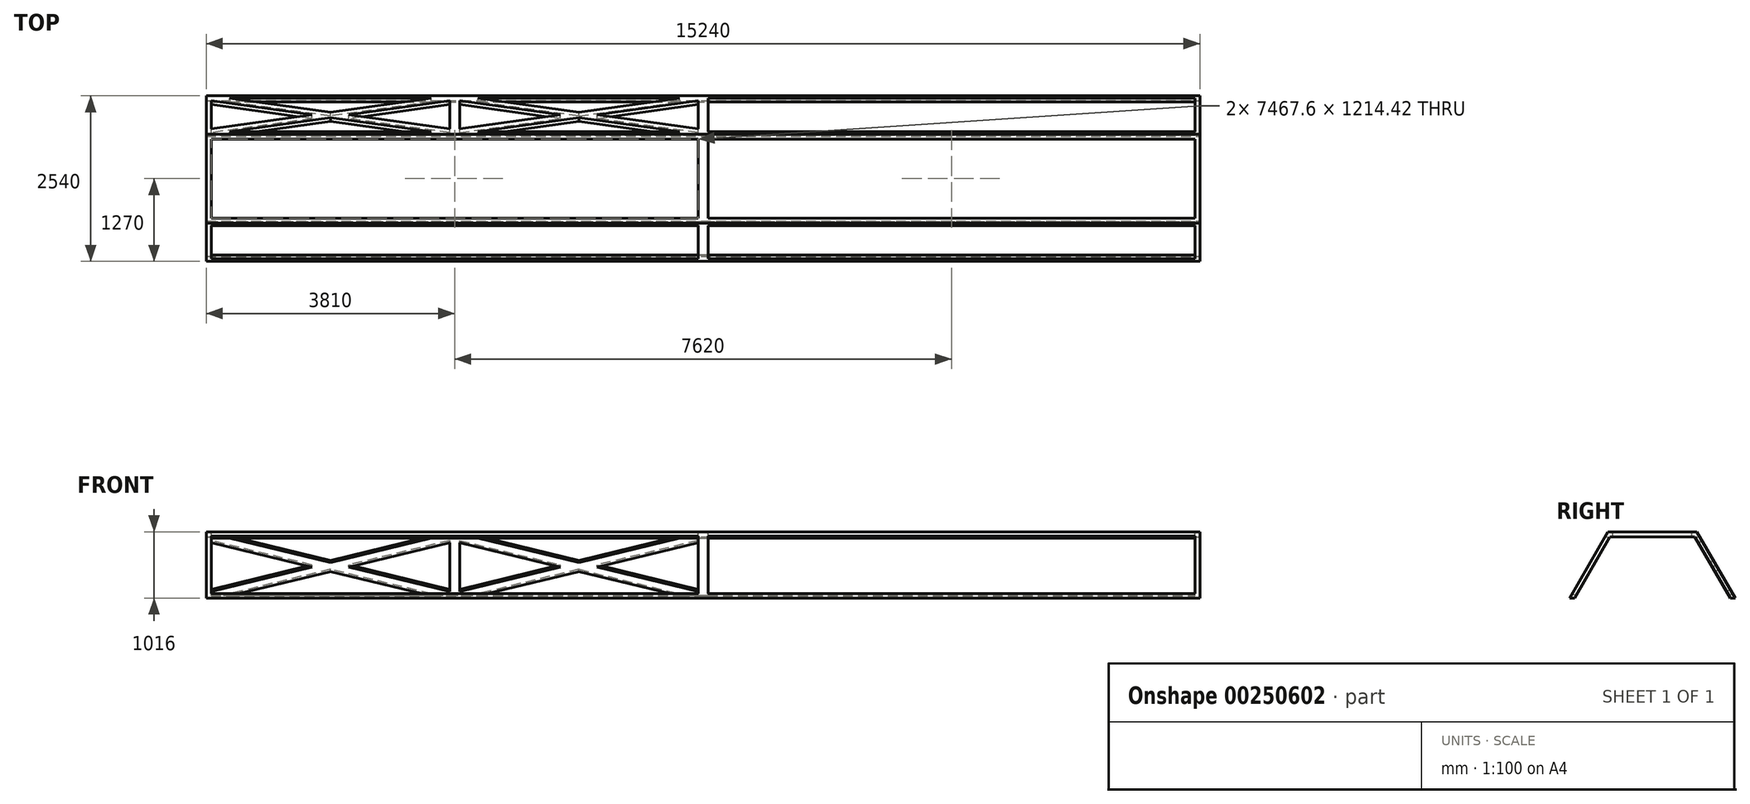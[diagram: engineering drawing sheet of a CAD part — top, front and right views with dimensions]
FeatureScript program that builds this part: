
annotation { "Feature Type Name" : "Feature", "Feature Type Description" : "" }
export const myFeature = defineFeature(function(context is Context, id is Id, definition is map)
    precondition{}
    {
        {
            var Q0;
            Q0=qCreatedBy(makeId("Right.planeOp"),FACE);
            var sketch = newSketch(context, id + "F0", { "sketchPlane" : qUnion([Q0])});
            skLineSegment(sketch, "E0", {"start": v(-627.03, 0) * mm, "end": v(-550.83, 0) * mm});
            skLineSegment(sketch, "E1", {"start": v(-627.03, 0) * mm, "end": v(-40.44, 1016) * mm});
            skLineSegment(sketch, "E2", {"start": v(-40.44, 1016) * mm, "end": v(1326.38, 1016) * mm});
            skLineSegment(sketch, "E3", {"start": v(-550.83, 0) * mm, "end": v(-8.23, 939.8) * mm});
            skLineSegment(sketch, "E4.MirrorCS", {"start": v(1836.77, 0) * mm, "end": v(1294.18, 939.8) * mm});
            skLineSegment(sketch, "E5.MirrorCS", {"start": v(1912.97, 0) * mm, "end": v(1326.38, 1016) * mm});
            skLineSegment(sketch, "E6", {"start": v(1912.97, 0) * mm, "end": v(1836.77, 0) * mm});
            skLineSegment(sketch, "E7.0", {"start": v(-8.23, 939.8) * mm, "end": v(1294.18, 939.8) * mm});
            skPoint(sketch, "E8.orphan", {"position": v(1250.18, 1016) * mm});
            skPoint(sketch, "E9.orphan", {"position": v(35.76, 1016) * mm});
            skPoint(sketch, "E10.orphan", {"position": v(642.97, 1016) * mm});
            skSolve(sketch);
        }
        {
            var Q0;
            Q0 = qSketchRegion(id + "F0", true);
            extrude(context, id + "F1", {"entities" : qUnion([Q0]), "oppositeDirection" : true, "depth" : 15240 * mm});
        }
        {
            var Q0;
            Q0=makeQuery(id+"F1.opExtrude","SWEPT_FACE",FACE,{"disambiguationData":[OSD([sQuery(id+"F0.wireOp",EDGE,"E1")])]});
            var sketch = newSketch(context, id + "F2", { "sketchPlane" : qUnion([Q0])});
            skLineSegment(sketch, "E11", {"start": v(-15240, 859.66) * mm, "end": v(0, 859.66) * mm});
            skLineSegment(sketch, "E12.0", {"start": v(-15163.8, 783.46) * mm, "end": v(-76.2, 783.46) * mm});
            skLineSegment(sketch, "E13", {"start": v(-15240, 859.66) * mm, "end": v(-15240, -313.51) * mm});
            skLineSegment(sketch, "E14.0", {"start": v(-15163.8, 783.46) * mm, "end": v(-15163.8, -237.31) * mm});
            skLineSegment(sketch, "E15", {"start": v(-15240, -313.51) * mm, "end": v(0, -313.51) * mm});
            skLineSegment(sketch, "E16.0", {"start": v(-15163.8, -237.31) * mm, "end": v(-76.2, -237.31) * mm});
            skLineSegment(sketch, "E17", {"start": v(0, 859.66) * mm, "end": v(0, -313.51) * mm});
            skLineSegment(sketch, "E18.0", {"start": v(-76.2, 783.46) * mm, "end": v(-76.2, -237.31) * mm});
            skSolve(sketch);
        }
        {
            var Q0;
            Q0=makeQuery(id+"F2.imprint","IMPRINT",FACE,{"disambiguationData":[TD([[makeQuery(id+"F2.imprint","IMPRINT",EDGE,{"derivedFrom":sQuery(id+"F2.wireOp",EDGE,"E12.0")}),-1.0]])]});
            extrude(context, id + "F3", {"entities" : qUnion([Q0]), "operationType" : NewBodyOperationType.REMOVE, "oppositeDirection" : true, "depth" : 76.2 * mm});
        }
        {
            var Q0;
            Q0=makeQuery(id+"F1.opExtrude","SWEPT_FACE",FACE,{"disambiguationData":[OSD([sQuery(id+"F0.wireOp",EDGE,"E2")])]});
            var sketch = newSketch(context, id + "F4", { "sketchPlane" : qUnion([Q0])});
            skLineSegment(sketch, "E19", {"start": v(-15240, 1326.38) * mm, "end": v(0, 1326.38) * mm});
            skLineSegment(sketch, "E20", {"start": v(0, 1326.38) * mm, "end": v(0, -40.44) * mm});
            skLineSegment(sketch, "E21", {"start": v(0, -40.44) * mm, "end": v(-15240, -40.44) * mm});
            skLineSegment(sketch, "E22", {"start": v(-15240, -40.44) * mm, "end": v(-15240, 1326.38) * mm});
            skLineSegment(sketch, "E23.0", {"start": v(-15163.8, 1250.18) * mm, "end": v(-76.2, 1250.18) * mm});
            skLineSegment(sketch, "E24.0", {"start": v(-15163.8, 35.76) * mm, "end": v(-15163.8, 1250.18) * mm});
            skLineSegment(sketch, "E25.0", {"start": v(-76.2, 35.76) * mm, "end": v(-15163.8, 35.76) * mm});
            skLineSegment(sketch, "E26.0", {"start": v(-76.2, 1250.18) * mm, "end": v(-76.2, 35.76) * mm});
            skSolve(sketch);
        }
        {
            var Q0;
            Q0=makeQuery(id+"F4.imprint","IMPRINT",FACE,{"disambiguationData":[TD([[makeQuery(id+"F4.imprint","IMPRINT",EDGE,{"derivedFrom":sQuery(id+"F4.wireOp",EDGE,"E23.0")}),-1.0]])]});
            extrude(context, id + "F5", {"entities" : qUnion([Q0]), "operationType" : NewBodyOperationType.REMOVE, "oppositeDirection" : true, "depth" : 76.2 * mm});
        }
        {
            var Q0;
            Q0=makeQuery(id+"F1.opExtrude","SWEPT_FACE",FACE,{"disambiguationData":[OSD([sQuery(id+"F0.wireOp",EDGE,"E5.MirrorCS")])]});
            var sketch = newSketch(context, id + "F6", { "sketchPlane" : qUnion([Q0])});
            skLineSegment(sketch, "E27", {"start": v(0, 216.69) * mm, "end": v(15240, 216.69) * mm});
            skLineSegment(sketch, "E28", {"start": v(15240, 216.69) * mm, "end": v(15240, -956.49) * mm});
            skLineSegment(sketch, "E29", {"start": v(15240, -956.49) * mm, "end": v(0, -956.49) * mm});
            skLineSegment(sketch, "E30", {"start": v(0, -956.49) * mm, "end": v(0, 216.69) * mm});
            skLineSegment(sketch, "E31.0", {"start": v(76.2, 140.49) * mm, "end": v(15163.8, 140.49) * mm});
            skLineSegment(sketch, "E32.0", {"start": v(76.2, -880.29) * mm, "end": v(76.2, 140.49) * mm});
            skLineSegment(sketch, "E33.0", {"start": v(15163.8, -880.29) * mm, "end": v(76.2, -880.29) * mm});
            skLineSegment(sketch, "E34.0", {"start": v(15163.8, 140.49) * mm, "end": v(15163.8, -880.29) * mm});
            skSolve(sketch);
        }
        {
            var Q0;
            Q0=makeQuery(id+"F6.imprint","IMPRINT",FACE,{"disambiguationData":[TD([[makeQuery(id+"F6.imprint","IMPRINT",EDGE,{"derivedFrom":sQuery(id+"F6.wireOp",EDGE,"E31.0")}),-1.0]])]});
            extrude(context, id + "F7", {"entities" : qUnion([Q0]), "operationType" : NewBodyOperationType.REMOVE, "oppositeDirection" : true, "depth" : 76.2 * mm});
        }
        {
            var Q0;
            Q0=makeQuery(id+"F1.opExtrude","SWEPT_FACE",FACE,{"disambiguationData":[OSD([sQuery(id+"F0.wireOp",EDGE,"E1")])]});
            var sketch = newSketch(context, id + "F8", { "sketchPlane" : qUnion([Q0])});
            skLineSegment(sketch, "E35", {"start": v(-7620, 783.46) * mm, "end": v(-7620, 228.8) * mm});
            skLineSegment(sketch, "E36", {"start": v(-7620, 228.8) * mm, "end": v(-7620, -237.31) * mm});
            skLineSegment(sketch, "E37", {"start": v(-7620, 783.46) * mm, "end": v(-7696.2, 783.46) * mm});
            skLineSegment(sketch, "E38", {"start": v(-7696.2, 783.46) * mm, "end": v(-7696.2, -237.31) * mm});
            skLineSegment(sketch, "E39", {"start": v(-7696.2, -237.31) * mm, "end": v(-7620, -237.31) * mm});
            skLineSegment(sketch, "E40", {"start": v(-7620, 783.46) * mm, "end": v(-7543.8, 783.46) * mm});
            skLineSegment(sketch, "E41", {"start": v(-7543.8, 783.46) * mm, "end": v(-7543.8, -237.31) * mm});
            skLineSegment(sketch, "E42", {"start": v(-7543.8, -237.31) * mm, "end": v(-7620, -237.31) * mm});
            skSolve(sketch);
        }
        {
            var Q0;
            Q0 = qSketchRegion(id + "F8", true);
            extrude(context, id + "F9", {"entities" : qUnion([Q0]), "operationType" : NewBodyOperationType.ADD, "oppositeDirection" : true, "depth" : 66.04 * mm});
        }
        {
            var Q0;
            Q0=makeQuery(id+"F1.opExtrude","SWEPT_FACE",FACE,{"disambiguationData":[OSD([sQuery(id+"F0.wireOp",EDGE,"E5.MirrorCS")])]});
            var sketch = newSketch(context, id + "F10", { "sketchPlane" : qUnion([Q0])});
            skLineSegment(sketch, "E43", {"start": v(7620, 140.49) * mm, "end": v(7620, -880.29) * mm});
            skLineSegment(sketch, "E44", {"start": v(7620, 140.49) * mm, "end": v(7543.8, 140.49) * mm});
            skLineSegment(sketch, "E45", {"start": v(7543.8, 140.49) * mm, "end": v(7543.8, -880.29) * mm});
            skLineSegment(sketch, "E46", {"start": v(7543.8, -880.29) * mm, "end": v(7620, -880.29) * mm});
            skLineSegment(sketch, "E47", {"start": v(7620, -880.29) * mm, "end": v(7696.2, -880.29) * mm});
            skLineSegment(sketch, "E48", {"start": v(7696.2, -880.29) * mm, "end": v(7696.2, 140.49) * mm});
            skLineSegment(sketch, "E49", {"start": v(7696.2, 140.49) * mm, "end": v(7620, 140.49) * mm});
            skSolve(sketch);
        }
        {
            var Q0;
            Q0 = qSketchRegion(id + "F10", true);
            extrude(context, id + "F11", {"entities" : qUnion([Q0]), "operationType" : NewBodyOperationType.ADD, "oppositeDirection" : true, "depth" : 66.04 * mm});
        }
        {
            var Q0;
            Q0=makeQuery(id+"F1.opExtrude","SWEPT_FACE",FACE,{"disambiguationData":[OSD([sQuery(id+"F0.wireOp",EDGE,"E2")])]});
            var sketch = newSketch(context, id + "F12", { "sketchPlane" : qUnion([Q0])});
            skLineSegment(sketch, "E50", {"start": v(-7620, 1250.18) * mm, "end": v(-7543.8, 1250.18) * mm});
            skLineSegment(sketch, "E51", {"start": v(-7543.8, 1250.18) * mm, "end": v(-7543.8, 35.76) * mm});
            skLineSegment(sketch, "E52", {"start": v(-7543.8, 35.76) * mm, "end": v(-7696.2, 35.76) * mm});
            skLineSegment(sketch, "E53", {"start": v(-7696.2, 35.76) * mm, "end": v(-7696.2, 1250.18) * mm});
            skLineSegment(sketch, "E54", {"start": v(-7696.2, 1250.18) * mm, "end": v(-7620, 1250.18) * mm});
            skSolve(sketch);
        }
        {
            var Q0;
            Q0 = qSketchRegion(id + "F12", true);
            extrude(context, id + "F13", {"entities" : qUnion([Q0]), "operationType" : NewBodyOperationType.ADD, "oppositeDirection" : true, "depth" : 76.2 * mm});
        }
        {
            var Q0;
            Q0=makeQuery(id+"F11.boolean.opBoolean","MERGE",FACE,{"derivedFrom":[makeQuery(id+"F1.opExtrude","SWEPT_FACE",FACE,{"disambiguationData":[OSD([sQuery(id+"F0.wireOp",EDGE,"E5.MirrorCS")])]}),makeQuery(id+"F11.opExtrude","CAP_FACE",FACE,{"disambiguationData":[OSD([sQuery(id+"F10.wireOp",EDGE,"E44"),sQuery(id+"F10.wireOp",EDGE,"E45"),sQuery(id+"F10.wireOp",EDGE,"E46"),sQuery(id+"F10.wireOp",EDGE,"E47"),sQuery(id+"F10.wireOp",EDGE,"E48"),sQuery(id+"F10.wireOp",EDGE,"E49")])],"isStart":true})]});
            var sketch = newSketch(context, id + "F14", { "sketchPlane" : qUnion([Q0])});
            skLineSegment(sketch, "E55.0", {"start": v(11353.8, 61.38) * mm, "end": v(11353.8, -801.17) * mm});
            skLineSegment(sketch, "E56.0", {"start": v(11506.2, 61.38) * mm, "end": v(11506.2, -801.17) * mm});
            skLineSegment(sketch, "E57.0", {"start": v(11070.33, 140.49) * mm, "end": v(9525, -290.79) * mm});
            skLineSegment(sketch, "E58.0", {"start": v(11353.8, 61.38) * mm, "end": v(9808.47, -369.9) * mm});
            skLineSegment(sketch, "E59.0", {"start": v(7696.2, 61.38) * mm, "end": v(9241.53, -369.9) * mm});
            skLineSegment(sketch, "E60.0", {"start": v(7979.67, 140.49) * mm, "end": v(9525, -290.79) * mm});
            skLineSegment(sketch, "E61.trimOffspring", {"start": v(9525, -449) * mm, "end": v(11070.33, -880.29) * mm});
            skLineSegment(sketch, "E62.trimOffspring", {"start": v(9808.47, -369.9) * mm, "end": v(11353.8, -801.17) * mm});
            skLineSegment(sketch, "E63.trimOffspring", {"start": v(9241.53, -369.9) * mm, "end": v(7696.2, -801.17) * mm});
            skLineSegment(sketch, "E64.trimOffspring", {"start": v(9525, -449) * mm, "end": v(7979.67, -880.29) * mm});
            skLineSegment(sketch, "E65", {"start": v(11353.8, -880.29) * mm, "end": v(11070.33, -880.29) * mm});
            skLineSegment(sketch, "E66", {"start": v(11353.8, 140.49) * mm, "end": v(11070.33, 140.49) * mm});
            skLineSegment(sketch, "E67", {"start": v(7696.2, 140.49) * mm, "end": v(7979.67, 140.49) * mm});
            skLineSegment(sketch, "E68", {"start": v(7696.2, 140.49) * mm, "end": v(7696.2, 61.38) * mm});
            skLineSegment(sketch, "E69", {"start": v(11353.8, -880.29) * mm, "end": v(11506.2, -880.29) * mm});
            skLineSegment(sketch, "E70", {"start": v(11353.8, 140.49) * mm, "end": v(11506.2, 140.49) * mm});
            skLineSegment(sketch, "E71", {"start": v(7696.2, -801.17) * mm, "end": v(7696.2, -880.29) * mm});
            skLineSegment(sketch, "E72", {"start": v(7696.2, -880.29) * mm, "end": v(7979.67, -880.29) * mm});
            skLineSegment(sketch, "E73.0", {"start": v(11506.2, 61.38) * mm, "end": v(13051.53, -369.9) * mm});
            skLineSegment(sketch, "E74.0", {"start": v(13618.47, -369.9) * mm, "end": v(15163.8, -801.17) * mm});
            skLineSegment(sketch, "E75.0", {"start": v(11789.67, -880.29) * mm, "end": v(13335, -449) * mm});
            skLineSegment(sketch, "E76.0", {"start": v(11506.2, -801.17) * mm, "end": v(13051.53, -369.9) * mm});
            skLineSegment(sketch, "E77", {"start": v(14880.33, 140.49) * mm, "end": v(15163.8, 140.49) * mm});
            skLineSegment(sketch, "E78", {"start": v(15163.8, 61.38) * mm, "end": v(15163.8, 140.49) * mm});
            skLineSegment(sketch, "E79", {"start": v(15163.8, -801.17) * mm, "end": v(15163.8, -880.29) * mm});
            skLineSegment(sketch, "E80", {"start": v(14880.33, -880.29) * mm, "end": v(15163.8, -880.29) * mm});
            skLineSegment(sketch, "E81", {"start": v(11506.2, -880.29) * mm, "end": v(11789.67, -880.29) * mm});
            skLineSegment(sketch, "E82", {"start": v(13335, -290.79) * mm, "end": v(11789.67, 140.49) * mm});
            skLineSegment(sketch, "E83", {"start": v(11506.2, 140.49) * mm, "end": v(11789.67, 140.49) * mm});
            skLineSegment(sketch, "E84.trimOffspring", {"start": v(13618.47, -369.9) * mm, "end": v(15163.8, 61.38) * mm});
            skLineSegment(sketch, "E85.trimOffspring", {"start": v(13335, -290.79) * mm, "end": v(14880.33, 140.49) * mm});
            skLineSegment(sketch, "E86.trimOffspring", {"start": v(13335, -449) * mm, "end": v(14880.33, -880.29) * mm});
            skSolve(sketch);
        }
        {
            var Q0;
            Q0 = qSketchRegion(id + "F14", true);
            extrude(context, id + "F15", {"entities" : qUnion([Q0]), "operationType" : NewBodyOperationType.ADD, "oppositeDirection" : true, "depth" : 66.04 * mm});
        }
    });
